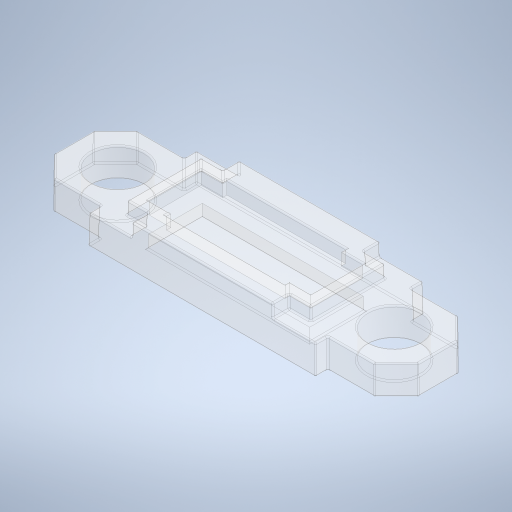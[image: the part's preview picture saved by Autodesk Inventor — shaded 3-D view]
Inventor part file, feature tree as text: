
AUTODESK INVENTOR PART (.ipt)
format: ipt  version: 2024.2 (Build 282272000, 272)  size: 459,264 bytes
history: native  units: in
note: dims shown in document units (in); Inventor stores cm internally (conversion verified against a paired STEP export)
features: fillet x1
ambient origin geometry x8: Origin, YZ Plane, XZ Plane, XY Plane, X Axis, Y Axis, Z Axis, Center Point
bodies: Solid1 (feature_tree)
feature tree (1):
  fillet  "Fillet1"  [1 undecoded]
note: 1 required parameter value undecoded (feature->parameter linkage not recoverable at this tier; creation-order binding heuristic only, values carry confidence <= 0.55)
